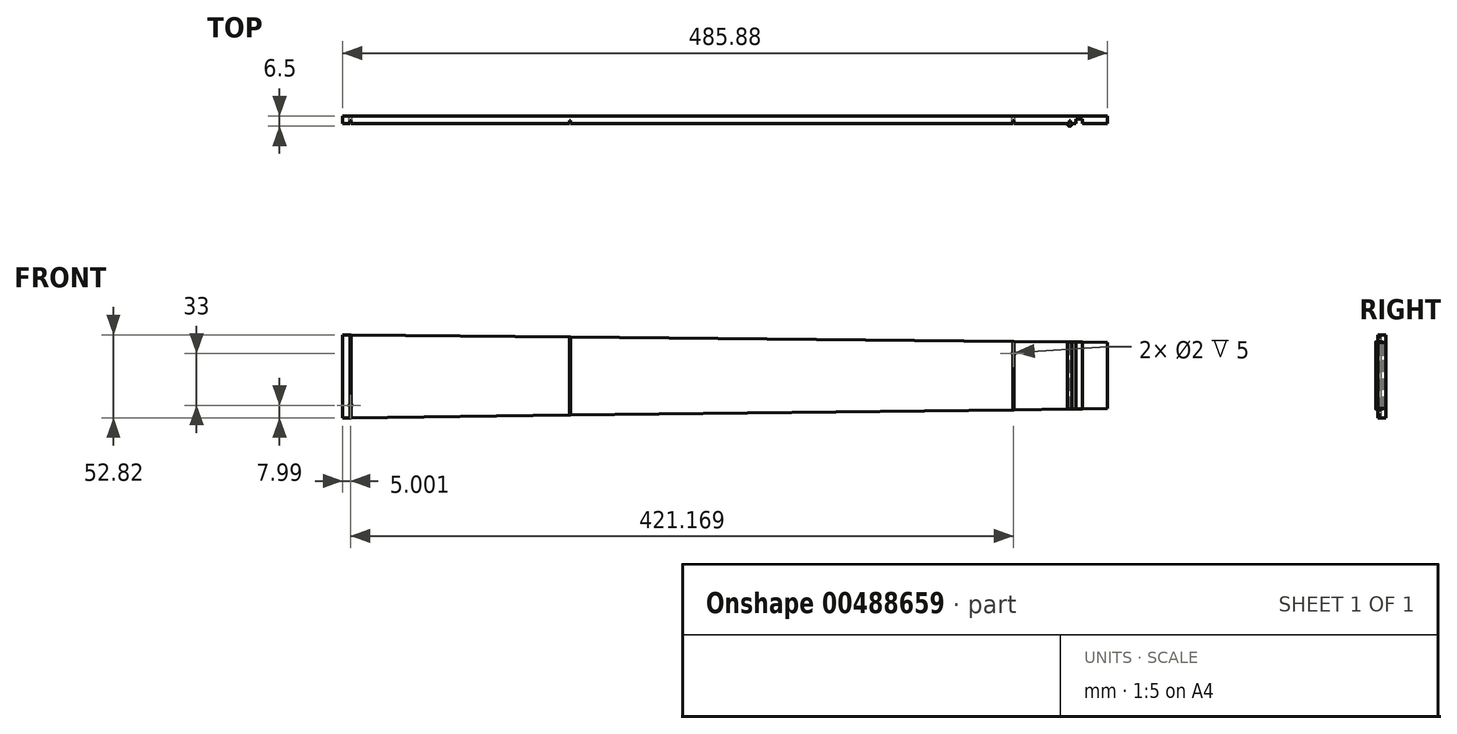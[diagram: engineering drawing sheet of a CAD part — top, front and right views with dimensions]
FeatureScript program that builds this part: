
annotation { "Feature Type Name" : "Feature", "Feature Type Description" : "" }
export const myFeature = defineFeature(function(context is Context, id is Id, definition is map)
    precondition{}
    {
        {
            var Q0;
            Q0=qCreatedBy(makeId("Front.planeOp"),FACE);
            var sketch = newSketch(context, id + "F0", { "sketchPlane" : qUnion([Q0])});
            skLineSegment(sketch, "E0", {"start": v(-350.77, 0) * mm, "end": v(570, 0) * mm});
            skLineSegment(sketch, "E1", {"start": v(317.5, 52.08) * mm, "end": v(317.5, 0) * mm});
            skLineSegment(sketch, "E2", {"start": v(0, 52.08) * mm, "end": v(0, 0) * mm});
            skLineSegment(sketch, "E3", {"start": v(-317.5, 0) * mm, "end": v(-317.5, 52.08) * mm});
            skLineSegment(sketch, "E4", {"start": v(-350.77, 52.08) * mm, "end": v(570, 52.08) * mm, "construction": true});
            skLineSegment(sketch, "E5", {"start": v(-139.3, 0) * mm, "end": v(-139.3, 52.08) * mm});
            skLineSegment(sketch, "E6", {"start": v(321.5, 52.08) * mm, "end": v(321.5, 0) * mm});
            skLineSegment(sketch, "E7", {"start": v(325.5, 52.08) * mm, "end": v(325.5, 0) * mm});
            skLineSegment(sketch, "E8", {"start": v(281.86, 52.08) * mm, "end": v(281.86, 0) * mm});
            skPoint(sketch, "E9", {"position": v(281.86, 15) * mm});
            skPoint(sketch, "E10", {"position": v(-139.3, -18) * mm});
            skSolve(sketch);
        }
        {
            var Q0;
            Q0=qCreatedBy(makeId("Front.planeOp"),FACE);
            var sketch = newSketch(context, id + "F1", { "sketchPlane" : qUnion([Q0])});
            skLineSegment(sketch, "E11", {"start": v(-317.5, 25.96) * mm, "end": v(-317.5, -25.96) * mm});
            skLineSegment(sketch, "E12", {"start": v(317.5, 19.66) * mm, "end": v(317.5, -18.3) * mm});
            skLineSegment(sketch, "E13", {"start": v(-317.5, 25.96) * mm, "end": v(505.53, 17.8) * mm, "construction": true});
            skLineSegment(sketch, "E14", {"start": v(-317.5, -25.96) * mm, "end": v(505, -16.04) * mm, "construction": true});
            skPoint(sketch, "E15", {"position": v(-317.5, 15.64) * mm});
            skPoint(sketch, "E16", {"position": v(-317.5, 5.24) * mm});
            skPoint(sketch, "E17", {"position": v(-317.5, -5.16) * mm});
            skPoint(sketch, "E18", {"position": v(-317.5, -15.56) * mm});
            skLineSegment(sketch, "E19", {"start": v(-317.5, 15.64) * mm, "end": v(504.34, 10.43) * mm, "construction": true});
            skLineSegment(sketch, "E20", {"start": v(-317.5, 5.24) * mm, "end": v(504.9, 3.41) * mm, "construction": true});
            skLineSegment(sketch, "E21", {"start": v(-317.5, -5.16) * mm, "end": v(504.85, -3.27) * mm, "construction": true});
            skLineSegment(sketch, "E22", {"start": v(-317.5, -15.56) * mm, "end": v(505.34, -9.71) * mm, "construction": true});
            skLineSegment(sketch, "E23", {"start": v(505.53, 18.38) * mm, "end": v(-317.5, 26.55) * mm});
            skLineSegment(sketch, "E24", {"start": v(-317.5, 25.38) * mm, "end": v(505.52, 17.2) * mm});
            skLineSegment(sketch, "E25", {"start": v(-317.5, 16.1) * mm, "end": v(504.34, 10.9) * mm});
            skLineSegment(sketch, "E26", {"start": v(-317.5, 15.18) * mm, "end": v(504.34, 9.98) * mm});
            skLineSegment(sketch, "E27", {"start": v(-317.5, 5.57) * mm, "end": v(504.9, 3.74) * mm});
            skLineSegment(sketch, "E28", {"start": v(504.9, 3.08) * mm, "end": v(-317.5, 4.9) * mm});
            skLineSegment(sketch, "E29", {"start": v(-317.5, -4.96) * mm, "end": v(504.85, -3.07) * mm});
            skLineSegment(sketch, "E30", {"start": v(-317.5, -5.36) * mm, "end": v(504.85, -3.48) * mm});
            skLineSegment(sketch, "E31", {"start": v(-317.5, -15.42) * mm, "end": v(505.34, -9.57) * mm});
            skLineSegment(sketch, "E32", {"start": v(505.34, -9.85) * mm, "end": v(-317.5, -15.7) * mm});
            skLineSegment(sketch, "E33", {"start": v(-317.5, -25.85) * mm, "end": v(505, -15.92) * mm});
            skLineSegment(sketch, "E34", {"start": v(505, -16.15) * mm, "end": v(-317.5, -26.08) * mm});
            skLineSegment(sketch, "E35", {"start": v(-317.5, 26.55) * mm, "end": v(-317.5, 25.38) * mm, "construction": true});
            skLineSegment(sketch, "E36", {"start": v(505.53, 18.38) * mm, "end": v(505.52, 17.2) * mm, "construction": true});
            skLineSegment(sketch, "E37", {"start": v(504.34, 10.9) * mm, "end": v(504.34, 9.98) * mm, "construction": true});
            skLineSegment(sketch, "E38", {"start": v(504.9, 3.74) * mm, "end": v(504.9, 3.08) * mm, "construction": true});
            skLineSegment(sketch, "E39", {"start": v(504.85, -3.07) * mm, "end": v(504.85, -3.48) * mm});
            skLineSegment(sketch, "E40", {"start": v(505.34, -9.57) * mm, "end": v(505.34, -9.85) * mm, "construction": true});
            skLineSegment(sketch, "E41", {"start": v(505, -15.92) * mm, "end": v(505, -16.15) * mm, "construction": true});
            skLineSegment(sketch, "E42", {"start": v(-317.5, 5.57) * mm, "end": v(-317.5, 4.9) * mm, "construction": true});
            skLineSegment(sketch, "E43", {"start": v(-317.5, -4.96) * mm, "end": v(-317.5, -5.36) * mm, "construction": true});
            skLineSegment(sketch, "E44", {"start": v(-317.5, -15.42) * mm, "end": v(-317.5, -15.7) * mm, "construction": true});
            skLineSegment(sketch, "E45", {"start": v(-317.5, -25.85) * mm, "end": v(-317.5, -26.08) * mm, "construction": true});
            skLineSegment(sketch, "E46", {"start": v(-317.5, 16.1) * mm, "end": v(-317.5, 15.18) * mm, "construction": true});
            skPoint(sketch, "E47", {"position": v(317.5, 19.07) * mm});
            skPoint(sketch, "E48", {"position": v(317.5, 12.07) * mm});
            skPoint(sketch, "E49", {"position": v(317.5, 11.16) * mm});
            skPoint(sketch, "E50", {"position": v(317.5, 4.16) * mm});
            skPoint(sketch, "E51", {"position": v(317.5, 3.5) * mm});
            skPoint(sketch, "E52", {"position": v(317.5, -3.5) * mm});
            skPoint(sketch, "E53", {"position": v(317.5, -3.9) * mm});
            skPoint(sketch, "E54", {"position": v(317.5, -10.9) * mm});
            skPoint(sketch, "E55", {"position": v(317.5, -11.19) * mm});
            skPoint(sketch, "E56", {"position": v(317.5, -18.19) * mm});
            skSolve(sketch);
        }
        {
            var Q0;
            Q0=qCreatedBy(makeId("Front.planeOp"),FACE);
            var sketch = newSketch(context, id + "F2", { "sketchPlane" : qUnion([Q0])});
            skLineSegment(sketch, "E57", {"start": v(-144.3, 26.83) * mm, "end": v(-144.3, -25.99) * mm});
            skLineSegment(sketch, "E58", {"start": v(-144.3, -25.99) * mm, "end": v(341.57, -20.12) * mm});
            skLineSegment(sketch, "E59", {"start": v(341.57, -20.12) * mm, "end": v(341.57, 22) * mm});
            skLineSegment(sketch, "E60", {"start": v(341.57, 22) * mm, "end": v(-144.3, 26.83) * mm});
            skPoint(sketch, "E61", {"position": v(-139.3, 24.2) * mm});
            skPoint(sketch, "E62", {"position": v(-139.3, -23.81) * mm});
            skSolve(sketch);
        }
        {
            var Q0;
            Q0 = qSketchRegion(id + "F2", true);
            extrude(context, id + "F3", {"entities" : qUnion([Q0]), "depth" : 5 * mm});
        }
        {
            var Q0;
            Q0=sQuery(id+"F0.wireOp",VERTEX,"E9");
            var Q1;
            Q1=sQuery(id+"F0.wireOp",VERTEX,"E10");
            var Q2;
            Q2=makeQuery(id+"F3.opExtrude","SWEPT_BODY",BODY,{"disambiguationData":[OSD([sQuery(id+"F2.wireOp",EDGE,"E57"),sQuery(id+"F2.wireOp",EDGE,"E58"),sQuery(id+"F2.wireOp",EDGE,"E59"),sQuery(id+"F2.wireOp",EDGE,"E60")])]});
            hole(context, id + "F4", {"style" : HoleStyle.SIMPLE, "endStyle" : HoleEndStyle.THROUGH, "oppositeDirection" : true, "holeDiameter" : 2 * mm, "isTappedThrough" : true, "tappedDepth" : 12 * mm, "tapClearance" : 3, "locations" : qUnion([Q0, Q1]), "scope" : qUnion([Q2])});
        }
        {
            var Q0;
            Q0=makeQuery(id+"F3.opExtrude","CAP_FACE",FACE,{"disambiguationData":[OSD([sQuery(id+"F2.wireOp",EDGE,"E57"),sQuery(id+"F2.wireOp",EDGE,"E58"),sQuery(id+"F2.wireOp",EDGE,"E59"),sQuery(id+"F2.wireOp",EDGE,"E60")])],"isStart":false});
            var sketch = newSketch(context, id + "F5", { "sketchPlane" : qUnion([Q0])});
            skLineSegment(sketch, "E63", {"start": v(317.5, 22.24) * mm, "end": v(317.5, -20.41) * mm});
            skArc(sketch, "E64.0.startCap", {"start": v(317.2, 22.24) * mm, "mid": v(317.5, 22.54) * mm, "end": v(317.8, 22.24) * mm});
            skArc(sketch, "E64.0.endCap", {"start": v(317.8, -20.41) * mm, "mid": v(317.5, -20.71) * mm, "end": v(317.2, -20.41) * mm});
            skLineSegment(sketch, "E64.0.left", {"start": v(317.8, 22.24) * mm, "end": v(317.8, -20.41) * mm});
            skLineSegment(sketch, "E64.0.right", {"start": v(317.2, 22.24) * mm, "end": v(317.2, -20.41) * mm});
            skLineSegment(sketch, "E65", {"start": v(281.86, 22.6) * mm, "end": v(281.86, -20.84) * mm});
            skArc(sketch, "E66.0.startCap", {"start": v(281.56, 22.6) * mm, "mid": v(281.86, 22.9) * mm, "end": v(282.16, 22.6) * mm});
            skArc(sketch, "E66.0.endCap", {"start": v(282.16, -20.84) * mm, "mid": v(281.86, -21.14) * mm, "end": v(281.56, -20.84) * mm});
            skLineSegment(sketch, "E66.0.left", {"start": v(282.16, 22.6) * mm, "end": v(282.16, -20.84) * mm});
            skLineSegment(sketch, "E66.0.right", {"start": v(281.56, 22.6) * mm, "end": v(281.56, -20.84) * mm});
            skLineSegment(sketch, "E67", {"start": v(-139.3, 26.78) * mm, "end": v(-139.3, -25.93) * mm});
            skLineSegment(sketch, "E68", {"start": v(0, 25.4) * mm, "end": v(0, -24.25) * mm});
            skArc(sketch, "E69.0.startCap", {"start": v(-0.3, 25.4) * mm, "mid": v(0, 25.7) * mm, "end": v(0.3, 25.4) * mm});
            skArc(sketch, "E69.0.endCap", {"start": v(0.3, -24.25) * mm, "mid": v(0, -24.55) * mm, "end": v(-0.3, -24.25) * mm});
            skLineSegment(sketch, "E69.0.left", {"start": v(0.3, 25.4) * mm, "end": v(0.3, -24.25) * mm});
            skLineSegment(sketch, "E69.0.right", {"start": v(-0.3, 25.4) * mm, "end": v(-0.3, -24.25) * mm});
            skArc(sketch, "E70.0.startCap", {"start": v(-139.6, 26.78) * mm, "mid": v(-139.3, 27.08) * mm, "end": v(-139, 26.78) * mm});
            skArc(sketch, "E70.0.endCap", {"start": v(-139, -25.93) * mm, "mid": v(-139.3, -26.23) * mm, "end": v(-139.6, -25.93) * mm});
            skLineSegment(sketch, "E70.0.left", {"start": v(-139, 26.78) * mm, "end": v(-139, -25.93) * mm});
            skLineSegment(sketch, "E70.0.right", {"start": v(-139.6, 26.78) * mm, "end": v(-139.6, -25.93) * mm});
            skSolve(sketch);
        }
        {
            var Q0;
            Q0 = qSketchRegion(id + "F5", true);
            extrude(context, id + "F6", {"entities" : qUnion([Q0]), "operationType" : NewBodyOperationType.REMOVE, "oppositeDirection" : true, "depth" : 2 * mm});
        }
        {
            var Q0;
            {var subQ5=makeQuery(id+"F3.opExtrude","CAP_EDGE",EDGE,{"disambiguationData":[OSD([sQuery(id+"F2.wireOp",EDGE,"E59")])],"isStart":false});Q0=makeQuery(id+"F5.imprint","IMPRINT",FACE,{"disambiguationData":[TD([[makeQuery(id+"F5.imprint","IMPRINT",EDGE,{"derivedFrom":subQ5}),1.0]])]});}
            var sketch = newSketch(context, id + "F7", { "sketchPlane" : qUnion([Q0])});
            skLineSegment(sketch, "E71", {"start": v(321.5, 22.2) * mm, "end": v(321.5, -20.37) * mm});
            skLineSegment(sketch, "E72", {"start": v(321.5, -20.37) * mm, "end": v(325.5, -20.32) * mm});
            skLineSegment(sketch, "E73", {"start": v(325.5, -20.32) * mm, "end": v(325.5, 22.16) * mm});
            skLineSegment(sketch, "E74", {"start": v(325.5, 22.16) * mm, "end": v(321.5, 22.2) * mm});
            skSolve(sketch);
        }
        {
            var Q0;
            Q0 = qSketchRegion(id + "F7", true);
            extrude(context, id + "F8", {"entities" : qUnion([Q0]), "operationType" : NewBodyOperationType.REMOVE, "oppositeDirection" : true, "depth" : 3 * mm});
        }
        {
            var Q0;
            Q0=qCreatedBy(makeId("Top.planeOp"),FACE);
            var sketch = newSketch(context, id + "F9", { "sketchPlane" : qUnion([Q0])});
            skLineSegment(sketch, "E75", {"start": v(317.2, -5) * mm, "end": v(317.2, -3) * mm});
            skLineSegment(sketch, "E76", {"start": v(317.2, -3) * mm, "end": v(317.8, -3) * mm});
            skLineSegment(sketch, "E77", {"start": v(317.8, -3) * mm, "end": v(317.8, -5) * mm});
            skLineSegment(sketch, "E78", {"start": v(317.8, -5) * mm, "end": v(319, -5) * mm});
            skLineSegment(sketch, "E79", {"start": v(317.2, -5) * mm, "end": v(316, -5) * mm});
            skArc(sketch, "E80", {"start": v(316, -5) * mm, "mid": v(317.5, -6.5) * mm, "end": v(319, -5) * mm});
            skSolve(sketch);
        }
        {
            var Q0;
            Q0 = qSketchRegion(id + "F9", true);
            var Q1;
            Q1=makeQuery(id+"F3.opExtrude","SWEPT_FACE",FACE,{"disambiguationData":[OSD([sQuery(id+"F2.wireOp",EDGE,"E58")])]});
            var Q2;
            Q2=makeQuery(id+"F3.opExtrude","SWEPT_FACE",FACE,{"disambiguationData":[OSD([sQuery(id+"F2.wireOp",EDGE,"E60")])]});
            extrude(context, id + "F10", {"entities" : qUnion([Q0]), "endBound" : BoundingType.UP_TO_SURFACE, "oppositeDirection" : true, "endBoundEntityFace" : qUnion([Q1]), "depth" : 25 * mm, "hasSecondDirection" : true, "secondDirectionBound" : SecondDirectionBoundingType.UP_TO_SURFACE, "secondDirectionOppositeDirection" : false, "secondDirectionBoundEntityFace" : qUnion([Q2]), "secondDirectionDepth" : 25 * mm});
        }
    });
